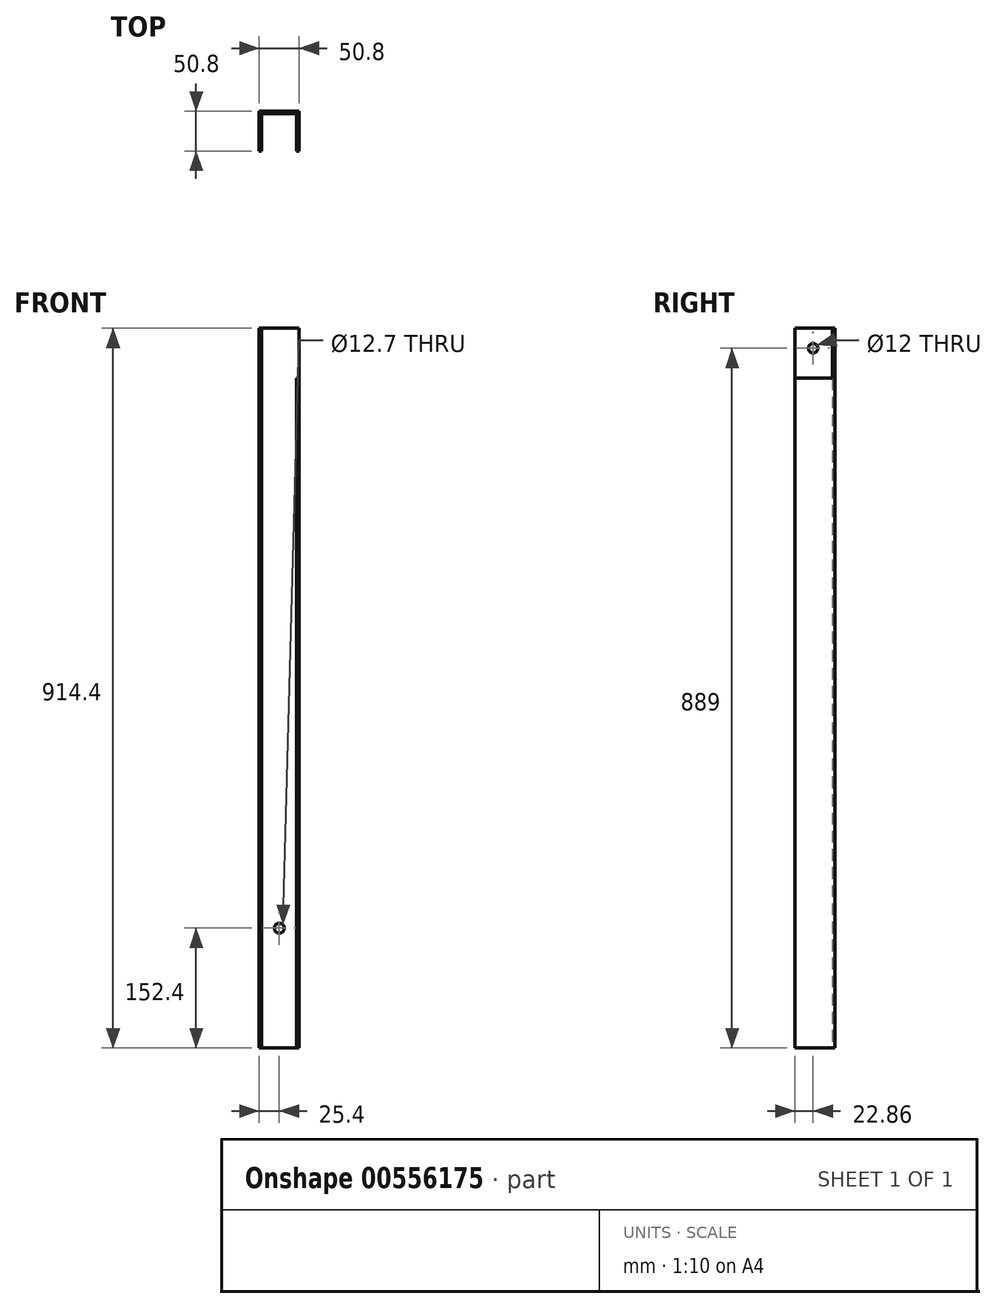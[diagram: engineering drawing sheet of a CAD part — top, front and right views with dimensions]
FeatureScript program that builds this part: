
annotation { "Feature Type Name" : "Feature", "Feature Type Description" : "" }
export const myFeature = defineFeature(function(context is Context, id is Id, definition is map)
    precondition{}
    {
        {
            var Q0;
            Q0=qCreatedBy(makeId("Top.planeOp"),FACE);
            var sketch = newSketch(context, id + "F0", { "sketchPlane" : qUnion([Q0])});
            skLineSegment(sketch, "E0.bottom", {"start": v(25.4, -25.4) * mm, "end": v(22.23, -25.4) * mm});
            skLineSegment(sketch, "E0.top", {"start": v(25.4, 25.4) * mm, "end": v(-25.4, 25.4) * mm});
            skLineSegment(sketch, "E0.left", {"start": v(25.4, -25.4) * mm, "end": v(25.4, 25.4) * mm});
            skLineSegment(sketch, "E0.right", {"start": v(-25.4, -25.4) * mm, "end": v(-25.4, 25.4) * mm});
            skPoint(sketch, "E0.middle", {"position": v(0, 0) * mm});
            skLineSegment(sketch, "E1.top", {"start": v(-22.23, 22.22) * mm, "end": v(22.23, 22.22) * mm});
            skLineSegment(sketch, "E1.left", {"start": v(-22.23, -25.4) * mm, "end": v(-22.23, 22.22) * mm});
            skLineSegment(sketch, "E1.right", {"start": v(22.23, -25.4) * mm, "end": v(22.23, 22.22) * mm});
            skLineSegment(sketch, "E2.trimOffspring", {"start": v(-22.22, -25.4) * mm, "end": v(-25.4, -25.4) * mm});
            skSolve(sketch);
        }
        {
            var Q0;
            Q0 = qSketchRegion(id + "F0", true);
            extrude(context, id + "F1", {"entities" : qUnion([Q0]), "depth" : 914.4 * mm, "offsetDistance" : 25.4 * mm});
        }
        {
            var Q0;
            Q0=makeQuery(id+"F1.opExtrude","SWEPT_FACE",FACE,{"disambiguationData":[OSD([sQuery(id+"F0.wireOp",EDGE,"E0.right")])]});
            var sketch = newSketch(context, id + "F2", { "sketchPlane" : qUnion([Q0])});
            skCircle(sketch, "E3", {"center": v(2.54, 889) * mm, "radius": 6 * mm});
            skSolve(sketch);
        }
        {
            var Q0;
            Q0 = qSketchRegion(id + "F2", true);
            extrude(context, id + "F3", {"entities" : qUnion([Q0]), "operationType" : NewBodyOperationType.REMOVE, "endBound" : BoundingType.UP_TO_NEXT, "oppositeDirection" : true, "depth" : 25.4 * mm, "offsetDistance" : 25.4 * mm});
        }
        {
            var Q0;
            Q0=makeQuery(id+"F1.opExtrude","SWEPT_FACE",FACE,{"disambiguationData":[OSD([sQuery(id+"F0.wireOp",EDGE,"E0.left")])]});
            var sketch = newSketch(context, id + "F4", { "sketchPlane" : qUnion([Q0])});
            skLineSegment(sketch, "E4", {"start": v(-25.4, 914.4) * mm, "end": v(22.22, 914.4) * mm});
            skLineSegment(sketch, "E5", {"start": v(22.22, 914.4) * mm, "end": v(22.23, 850.9) * mm});
            skLineSegment(sketch, "E6", {"start": v(22.23, 850.9) * mm, "end": v(-25.4, 850.9) * mm});
            skLineSegment(sketch, "E7", {"start": v(-25.4, 850.9) * mm, "end": v(-25.4, 914.4) * mm});
            skSolve(sketch);
        }
        {
            var Q0;
            Q0 = qSketchRegion(id + "F4", true);
            extrude(context, id + "F5", {"entities" : qUnion([Q0]), "operationType" : NewBodyOperationType.REMOVE, "oppositeDirection" : true, "depth" : 25.4 * mm, "offsetDistance" : 25.4 * mm});
        }
        {
            var Q0;
            Q0=makeQuery(id+"F1.opExtrude","SWEPT_FACE",FACE,{"disambiguationData":[OSD([sQuery(id+"F0.wireOp",EDGE,"E0.top")])]});
            var sketch = newSketch(context, id + "F6", { "sketchPlane" : qUnion([Q0])});
            skLineSegment(sketch, "E8", {"start": v(-25.4, 0) * mm, "end": v(-25.4, 914.4) * mm, "construction": true});
            skLineSegment(sketch, "E9", {"start": v(-25.4, 457.2) * mm, "end": v(25.4, 457.2) * mm, "construction": true});
            skLineSegment(sketch, "E10", {"start": v(0, 457.2) * mm, "end": v(0, 152.4) * mm, "construction": true});
            skCircle(sketch, "E11", {"center": v(0, 152.4) * mm, "radius": 6.35 * mm});
            skSolve(sketch);
        }
        {
            var Q0;
            Q0 = qSketchRegion(id + "F6", true);
            extrude(context, id + "F7", {"entities" : qUnion([Q0]), "operationType" : NewBodyOperationType.REMOVE, "oppositeDirection" : true, "depth" : 25.4 * mm, "offsetDistance" : 25.4 * mm});
        }
    });
